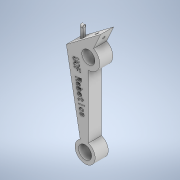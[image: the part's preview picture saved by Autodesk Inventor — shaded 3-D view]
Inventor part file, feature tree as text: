
AUTODESK INVENTOR PART (.ipt)
format: ipt  version: 2022 (Build 260153000, 153)  size: 469,504 bytes
history: native  units: in
note: dims shown in document units (in); Inventor stores cm internally (conversion verified against a paired STEP export)
features: extrude x4, sketch x4
ambient origin geometry x8: Origin, YZ Plane, XZ Plane, XY Plane, X Axis, Y Axis, Z Axis, Center Point
bodies: Solid1 (feature_tree)
feature tree (8):
  extrude  "Extrusion1"  Depth=0.4in
  extrude  "Extrusion2"  Depth=0.52in
  extrude  "Extrusion3"  TaperAngle=0.0deg  [1 undecoded]
  extrude  "Extrusion4"  Depth=0.1in
  sketch  "Sketch1"  dims[d2=6.0in d3=0.4in]
  sketch  "Sketch2"  dims[d4=0.52in d5=0.52in]
  sketch  "Sketch3"  dims[d6=0.52in d7=0.0in]
  sketch  "Sketch4"  dims[d8=1.355in d9=0.0in d10=0.1in d11=4.145in d12=0.0in d13=0.105in d14=0.0in d15=0.5in d16=0.0344in]
note: 1 required parameter value undecoded (feature->parameter linkage not recoverable at this tier; creation-order binding heuristic only, values carry confidence <= 0.55)
